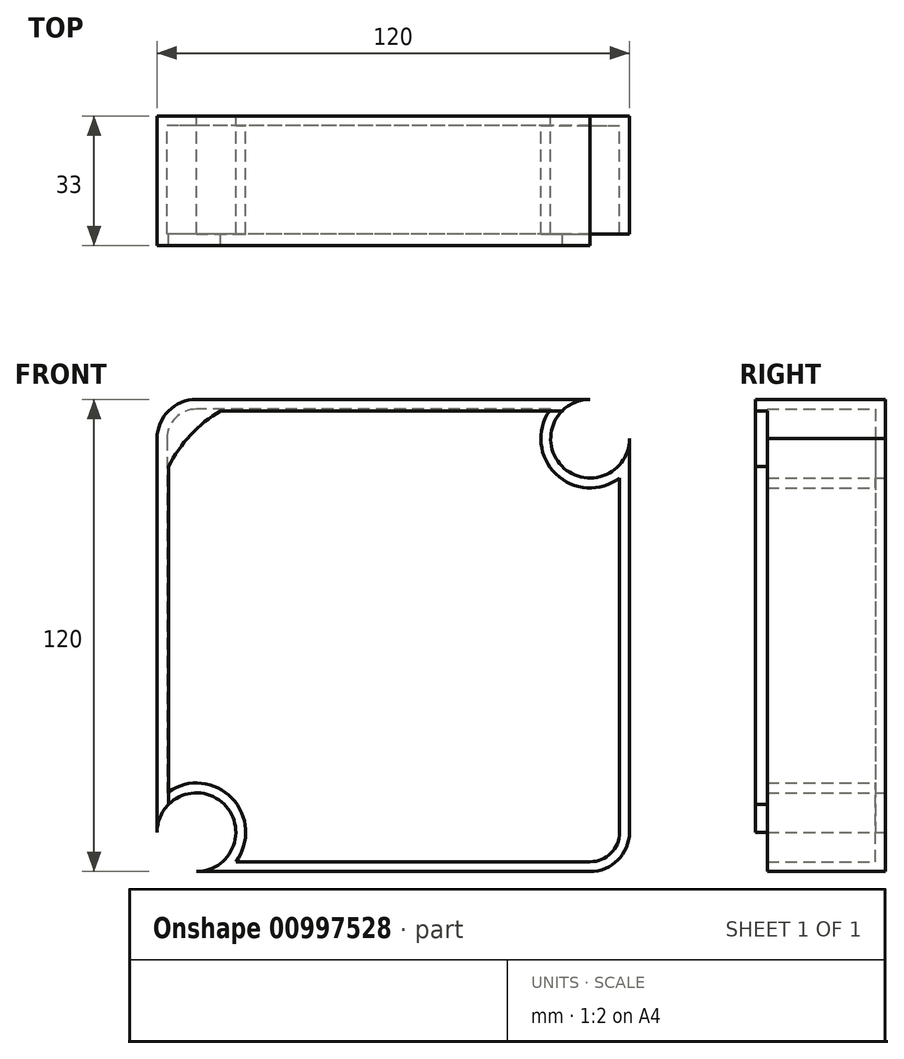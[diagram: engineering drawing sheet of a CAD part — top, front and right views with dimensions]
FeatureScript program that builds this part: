
annotation { "Feature Type Name" : "Feature", "Feature Type Description" : "" }
export const myFeature = defineFeature(function(context is Context, id is Id, definition is map)
    precondition{}
    {
        {
            var Q0;
            Q0=qCreatedBy(makeId("Front.planeOp"),FACE);
            var sketch = newSketch(context, id + "F0", { "sketchPlane" : qUnion([Q0])});
            skLineSegment(sketch, "E0.bottom", {"start": v(50, 60) * mm, "end": v(-50, 60) * mm});
            skLineSegment(sketch, "E0.top", {"start": v(50, -60) * mm, "end": v(-50, -60) * mm});
            skLineSegment(sketch, "E0.left", {"start": v(60, 50) * mm, "end": v(60, -50) * mm});
            skLineSegment(sketch, "E0.right", {"start": v(-60, 50) * mm, "end": v(-60, -50) * mm});
            skPoint(sketch, "E0.middle", {"position": v(0, 0) * mm});
            skLineSegment(sketch, "E1", {"start": v(-60, 0) * mm, "end": v(-60, 50) * mm});
            skLineSegment(sketch, "E2.MirrorCS", {"start": v(0, 60) * mm, "end": v(-50, 60) * mm});
            skArc(sketch, "E3", {"start": v(-50, 60) * mm, "mid": v(-57.07, 57.07) * mm, "end": v(-60, 50) * mm});
            skPoint(sketch, "E4.orphan", {"position": v(-60, 60) * mm});
            skArc(sketch, "E5.MirrorCS", {"start": v(50, 60) * mm, "mid": v(57.07, 57.07) * mm, "end": v(60, 50) * mm});
            skArc(sketch, "E6.MirrorCS", {"start": v(-50, -60) * mm, "mid": v(-57.07, -57.07) * mm, "end": v(-60, -50) * mm});
            skArc(sketch, "E7.MirrorCS", {"start": v(50, -60) * mm, "mid": v(57.07, -57.07) * mm, "end": v(60, -50) * mm});
            skPoint(sketch, "E8.orphan", {"position": v(60, 60) * mm});
            skPoint(sketch, "E9.orphan", {"position": v(60, -60) * mm});
            skPoint(sketch, "E10.orphan", {"position": v(-60, -60) * mm});
            skCircle(sketch, "E11", {"center": v(-50, 50) * mm, "radius": 10 * mm});
            skCircle(sketch, "E12.MirrorC", {"center": v(50, 50) * mm, "radius": 10 * mm});
            skCircle(sketch, "E13.MirrorC", {"center": v(-50, -50) * mm, "radius": 10 * mm});
            skCircle(sketch, "E14.MirrorC", {"center": v(50, -50) * mm, "radius": 10 * mm});
            skSolve(sketch);
        }
        {
            var Q0;
            {var subQ4=sQuery(id+"F0.wireOp",EDGE,"E0.bottom");Q0=makeQuery(id+"F0.imprint","IMPRINT",FACE,{"disambiguationData":[TD([[makeQuery(id+"F0.imprint","IMPRINT",EDGE,{"derivedFrom":subQ4}),1.0]])]});}
            var Q1;
            {var subQ0=sQuery(id+"F0.wireOp",EDGE,"E11");var subQ1=makeQuery(id+"F0.imprint","INTERSECT",VERTEX,{"derivedFrom":[sQuery(id+"F0.wireOp",EDGE,"E1"),subQ0]});Q1=makeQuery(id+"F0.imprint","IMPRINT",FACE,{"disambiguationData":[TD([[makeQuery(id+"F0.imprint","IMPRINT",EDGE,{"disambiguationData":[TD([[subQ1,1.0]])],"derivedFrom":subQ0}),1.0]])]});}
            var Q2;
            {var subQ0=sQuery(id+"F0.wireOp",EDGE,"E13.MirrorC");var subQ1=makeQuery(id+"F0.imprint","INTERSECT",VERTEX,{"derivedFrom":[sQuery(id+"F0.wireOp",EDGE,"E0.top"),subQ0]});Q2=makeQuery(id+"F0.imprint","IMPRINT",FACE,{"disambiguationData":[TD([[makeQuery(id+"F0.imprint","IMPRINT",EDGE,{"disambiguationData":[TD([[subQ1,-1.0]])],"derivedFrom":subQ0}),-1.0]])]});}
            var Q3;
            {var subQ0=sQuery(id+"F0.wireOp",EDGE,"E14.MirrorC");var subQ1=makeQuery(id+"F0.imprint","INTERSECT",VERTEX,{"derivedFrom":[sQuery(id+"F0.wireOp",EDGE,"E0.top"),subQ0]});Q3=makeQuery(id+"F0.imprint","IMPRINT",FACE,{"disambiguationData":[TD([[makeQuery(id+"F0.imprint","IMPRINT",EDGE,{"disambiguationData":[TD([[subQ1,-1.0]])],"derivedFrom":subQ0}),1.0]])]});}
            var Q4;
            {var subQ0=sQuery(id+"F0.wireOp",EDGE,"E12.MirrorC");var subQ1=makeQuery(id+"F0.imprint","INTERSECT",VERTEX,{"derivedFrom":[sQuery(id+"F0.wireOp",EDGE,"E0.bottom"),subQ0]});Q4=makeQuery(id+"F0.imprint","IMPRINT",FACE,{"disambiguationData":[TD([[makeQuery(id+"F0.imprint","IMPRINT",EDGE,{"disambiguationData":[TD([[subQ1,-1.0]])],"derivedFrom":subQ0}),-1.0]])]});}
            extrude(context, id + "F1", {"entities" : qUnion([Q0, Q1, Q2, Q3, Q4]), "depth" : 25 * mm, "offsetDistance" : 25 * mm});
        }
        {
            var Q0;
            {var subQ0=sQuery(id+"F0.wireOp",EDGE,"E11");var subQ1=makeQuery(id+"F0.imprint","INTERSECT",VERTEX,{"derivedFrom":[sQuery(id+"F0.wireOp",EDGE,"E1"),subQ0]});Q0=makeQuery(id+"F0.imprint","IMPRINT",FACE,{"disambiguationData":[TD([[makeQuery(id+"F0.imprint","IMPRINT",EDGE,{"disambiguationData":[TD([[subQ1,1.0]])],"derivedFrom":subQ0}),1.0]])]});}
            var Q1;
            {var subQ0=sQuery(id+"F0.wireOp",EDGE,"E12.MirrorC");var subQ1=makeQuery(id+"F0.imprint","INTERSECT",VERTEX,{"derivedFrom":[sQuery(id+"F0.wireOp",EDGE,"E0.bottom"),subQ0]});Q1=makeQuery(id+"F0.imprint","IMPRINT",FACE,{"disambiguationData":[TD([[makeQuery(id+"F0.imprint","IMPRINT",EDGE,{"disambiguationData":[TD([[subQ1,-1.0]])],"derivedFrom":subQ0}),-1.0]])]});}
            var Q2;
            {var subQ0=sQuery(id+"F0.wireOp",EDGE,"E14.MirrorC");var subQ1=makeQuery(id+"F0.imprint","INTERSECT",VERTEX,{"derivedFrom":[sQuery(id+"F0.wireOp",EDGE,"E0.top"),subQ0]});Q2=makeQuery(id+"F0.imprint","IMPRINT",FACE,{"disambiguationData":[TD([[makeQuery(id+"F0.imprint","IMPRINT",EDGE,{"disambiguationData":[TD([[subQ1,-1.0]])],"derivedFrom":subQ0}),1.0]])]});}
            var Q3;
            {var subQ0=sQuery(id+"F0.wireOp",EDGE,"E13.MirrorC");var subQ1=makeQuery(id+"F0.imprint","INTERSECT",VERTEX,{"derivedFrom":[sQuery(id+"F0.wireOp",EDGE,"E0.top"),subQ0]});Q3=makeQuery(id+"F0.imprint","IMPRINT",FACE,{"disambiguationData":[TD([[makeQuery(id+"F0.imprint","IMPRINT",EDGE,{"disambiguationData":[TD([[subQ1,-1.0]])],"derivedFrom":subQ0}),-1.0]])]});}
            extrude(context, id + "F2", {"entities" : qUnion([Q0, Q1, Q2, Q3]), "operationType" : NewBodyOperationType.ADD, "depth" : -5 * mm, "offsetDistance" : 25 * mm});
        }
        {
            var Q0;
            Q0=makeQuery(id+"F1.opExtrude","CAP_FACE",FACE,{"disambiguationData":[OSD([sQuery(id+"F0.wireOp",EDGE,"E0.bottom"),sQuery(id+"F0.wireOp",EDGE,"E0.top"),sQuery(id+"F0.wireOp",EDGE,"E0.left"),sQuery(id+"F0.wireOp",EDGE,"E0.right"),sQuery(id+"F0.wireOp",EDGE,"E1"),sQuery(id+"F0.wireOp",EDGE,"E2.MirrorCS"),sQuery(id+"F0.wireOp",EDGE,"E11"),sQuery(id+"F0.wireOp",EDGE,"E12.MirrorC"),sQuery(id+"F0.wireOp",EDGE,"E13.MirrorC"),sQuery(id+"F0.wireOp",EDGE,"E14.MirrorC")])],"isStart":false});
            var sketch = newSketch(context, id + "F3", { "sketchPlane" : qUnion([Q0])});
            skLineSegment(sketch, "E15.bottom", {"start": v(43.83, 57.07) * mm, "end": v(-43.83, 57.07) * mm});
            skLineSegment(sketch, "E15.top", {"start": v(43.83, -57.07) * mm, "end": v(-43.83, -57.07) * mm});
            skLineSegment(sketch, "E15.left", {"start": v(57.07, 42.94) * mm, "end": v(57.07, -42.94) * mm});
            skLineSegment(sketch, "E15.right", {"start": v(-57.07, 42.94) * mm, "end": v(-57.07, -42.94) * mm});
            skPoint(sketch, "E15.middle", {"position": v(0, 0) * mm});
            skArc(sketch, "E16", {"start": v(-43.83, 57.07) * mm, "mid": v(-51.48, 50.97) * mm, "end": v(-57.07, 42.94) * mm});
            skPoint(sketch, "E17.orphan", {"position": v(-57.07, 57.07) * mm});
            skArc(sketch, "E18.MirrorCS", {"start": v(43.83, 57.07) * mm, "mid": v(51.48, 50.97) * mm, "end": v(57.07, 42.94) * mm});
            skArc(sketch, "E19.MirrorCS", {"start": v(-43.83, -57.07) * mm, "mid": v(-51.48, -50.97) * mm, "end": v(-57.07, -42.94) * mm});
            skArc(sketch, "E20.MirrorCS", {"start": v(43.83, -57.07) * mm, "mid": v(51.48, -50.97) * mm, "end": v(57.07, -42.94) * mm});
            skPoint(sketch, "E21.orphan", {"position": v(57.07, 57.07) * mm});
            skPoint(sketch, "E22.orphan", {"position": v(57.07, -57.07) * mm});
            skPoint(sketch, "E23.orphan", {"position": v(-57.07, -57.07) * mm});
            skSolve(sketch);
        }
        {
            var Q0;
            Q0=makeQuery(id+"F1.opExtrude","CAP_FACE",FACE,{"disambiguationData":[OSD([sQuery(id+"F0.wireOp",EDGE,"E0.bottom"),sQuery(id+"F0.wireOp",EDGE,"E0.top"),sQuery(id+"F0.wireOp",EDGE,"E0.left"),sQuery(id+"F0.wireOp",EDGE,"E0.right"),sQuery(id+"F0.wireOp",EDGE,"E1"),sQuery(id+"F0.wireOp",EDGE,"E2.MirrorCS"),sQuery(id+"F0.wireOp",EDGE,"E11"),sQuery(id+"F0.wireOp",EDGE,"E12.MirrorC"),sQuery(id+"F0.wireOp",EDGE,"E13.MirrorC"),sQuery(id+"F0.wireOp",EDGE,"E14.MirrorC")])],"isStart":false});
            shell(context, id + "F4", {"entities" : qUnion([Q0]), "thickness" : 2.5 * mm});
        }
        {
            var Q0;
            Q0=makeQuery(id+"F3.imprint","IMPRINT",FACE,{"disambiguationData":[TD([[makeQuery(id+"F3.imprint","IMPRINT",EDGE,{"derivedFrom":sQuery(id+"F3.wireOp",EDGE,"E15.bottom")}),-1.0]])]});
            extrude(context, id + "F5", {"entities" : qUnion([Q0]), "operationType" : NewBodyOperationType.ADD, "depth" : 3 * mm, "offsetDistance" : 25 * mm});
        }
    });
